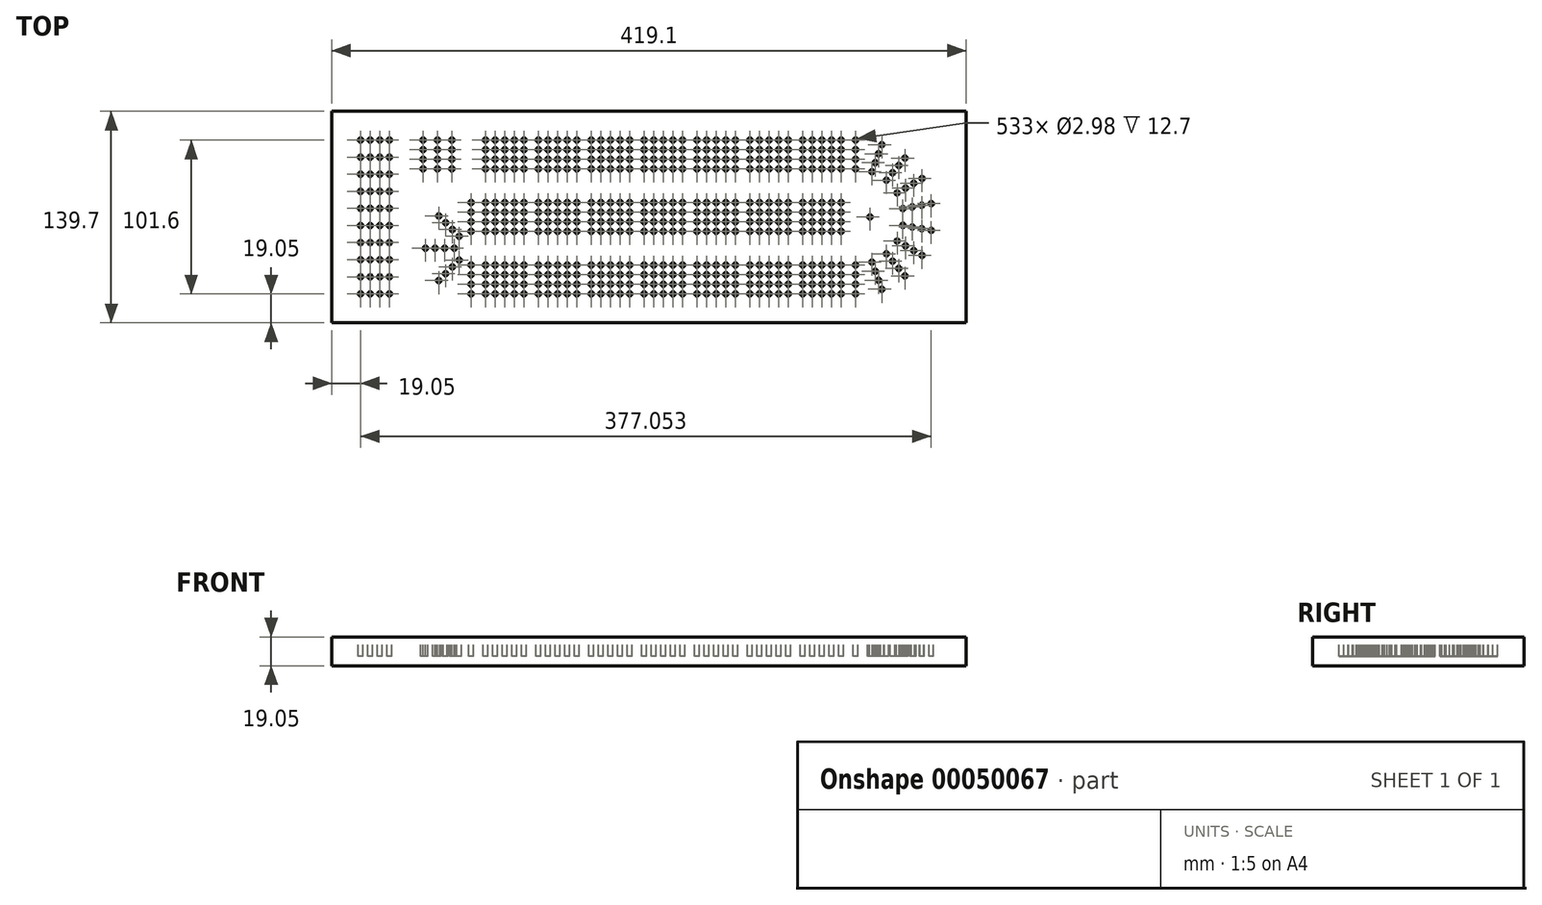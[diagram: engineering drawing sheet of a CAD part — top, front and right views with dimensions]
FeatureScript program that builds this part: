
annotation { "Feature Type Name" : "Feature", "Feature Type Description" : "" }
export const myFeature = defineFeature(function(context is Context, id is Id, definition is map)
    precondition{}
    {
        {
            var Q0;
            Q0=qCreatedBy(makeId("Top.planeOp"),FACE);
            var sketch = newSketch(context, id + "F0", { "sketchPlane" : qUnion([Q0])});
            skLineSegment(sketch, "E0.bottom", {"start": v(0, 0) * mm, "end": v(419.1, 0) * mm});
            skLineSegment(sketch, "E0.top", {"start": v(0, 139.7) * mm, "end": v(419.1, 139.7) * mm});
            skLineSegment(sketch, "E0.left", {"start": v(0, 0) * mm, "end": v(0, 139.7) * mm});
            skLineSegment(sketch, "E0.right", {"start": v(419.1, 0) * mm, "end": v(419.1, 139.7) * mm});
            skSolve(sketch);
        }
        {
            var Q0;
            Q0=qSketchRegion(id+"F0",true);
            extrude(context, id + "F1", {"entities" : qUnion([Q0]), "depth" : 19.05 * mm});
        }
        {
            var Q0;
            Q0=makeQuery(id+"F1.opExtrude","CAP_FACE",FACE,{"disambiguationData":[OSD([sQuery(id+"F0.wireOp",EDGE,"E0.bottom"),sQuery(id+"F0.wireOp",EDGE,"E0.top"),sQuery(id+"F0.wireOp",EDGE,"E0.left"),sQuery(id+"F0.wireOp",EDGE,"E0.right")])],"isStart":false});
            var sketch = newSketch(context, id + "F2", { "sketchPlane" : qUnion([Q0])});
            skLineSegment(sketch, "E1", {"start": v(19.05, 139.7) * mm, "end": v(19.05, 120.65) * mm});
            skLineSegment(sketch, "E2", {"start": v(19.05, 120.65) * mm, "end": v(0, 120.65) * mm});
            skCircle(sketch, "E3", {"center": v(19.05, 120.65) * mm, "radius": 1.49 * mm});
            skCircle(sketch, "E4.0.1.0", {"center": v(19.05, 109.36) * mm, "radius": 1.49 * mm});
            skCircle(sketch, "E4.0.2.0", {"center": v(19.05, 98.07) * mm, "radius": 1.49 * mm});
            skCircle(sketch, "E4.0.3.0", {"center": v(19.05, 86.78) * mm, "radius": 1.49 * mm});
            skCircle(sketch, "E4.0.4.0", {"center": v(19.05, 75.5) * mm, "radius": 1.49 * mm});
            skCircle(sketch, "E4.0.5.0", {"center": v(19.05, 64.2) * mm, "radius": 1.49 * mm});
            skCircle(sketch, "E4.0.6.0", {"center": v(19.05, 52.92) * mm, "radius": 1.49 * mm});
            skCircle(sketch, "E4.0.7.0", {"center": v(19.05, 41.63) * mm, "radius": 1.49 * mm});
            skCircle(sketch, "E4.0.8.0", {"center": v(19.05, 30.34) * mm, "radius": 1.49 * mm});
            skCircle(sketch, "E4.0.9.0", {"center": v(19.05, 19.05) * mm, "radius": 1.49 * mm});
            skCircle(sketch, "E4.1.0.0", {"center": v(25.4, 120.65) * mm, "radius": 1.49 * mm});
            skCircle(sketch, "E4.1.1.0", {"center": v(25.4, 109.36) * mm, "radius": 1.49 * mm});
            skCircle(sketch, "E4.1.2.0", {"center": v(25.4, 98.07) * mm, "radius": 1.49 * mm});
            skCircle(sketch, "E4.1.3.0", {"center": v(25.4, 86.78) * mm, "radius": 1.49 * mm});
            skCircle(sketch, "E4.1.4.0", {"center": v(25.4, 75.5) * mm, "radius": 1.49 * mm});
            skCircle(sketch, "E4.1.5.0", {"center": v(25.4, 64.2) * mm, "radius": 1.49 * mm});
            skCircle(sketch, "E4.1.6.0", {"center": v(25.4, 52.92) * mm, "radius": 1.49 * mm});
            skCircle(sketch, "E4.1.7.0", {"center": v(25.4, 41.63) * mm, "radius": 1.49 * mm});
            skCircle(sketch, "E4.1.8.0", {"center": v(25.4, 30.34) * mm, "radius": 1.49 * mm});
            skCircle(sketch, "E4.1.9.0", {"center": v(25.4, 19.05) * mm, "radius": 1.49 * mm});
            skCircle(sketch, "E4.2.0.0", {"center": v(31.75, 120.65) * mm, "radius": 1.49 * mm});
            skCircle(sketch, "E4.2.1.0", {"center": v(31.75, 109.36) * mm, "radius": 1.49 * mm});
            skCircle(sketch, "E4.2.2.0", {"center": v(31.75, 98.07) * mm, "radius": 1.49 * mm});
            skCircle(sketch, "E4.2.3.0", {"center": v(31.75, 86.78) * mm, "radius": 1.49 * mm});
            skCircle(sketch, "E4.2.4.0", {"center": v(31.75, 75.5) * mm, "radius": 1.49 * mm});
            skCircle(sketch, "E4.2.5.0", {"center": v(31.75, 64.2) * mm, "radius": 1.49 * mm});
            skCircle(sketch, "E4.2.6.0", {"center": v(31.75, 52.92) * mm, "radius": 1.49 * mm});
            skCircle(sketch, "E4.2.7.0", {"center": v(31.75, 41.63) * mm, "radius": 1.49 * mm});
            skCircle(sketch, "E4.2.8.0", {"center": v(31.75, 30.34) * mm, "radius": 1.49 * mm});
            skCircle(sketch, "E4.2.9.0", {"center": v(31.75, 19.05) * mm, "radius": 1.49 * mm});
            skCircle(sketch, "E4.3.0.0", {"center": v(38.1, 120.65) * mm, "radius": 1.49 * mm});
            skCircle(sketch, "E4.3.1.0", {"center": v(38.1, 109.36) * mm, "radius": 1.49 * mm});
            skCircle(sketch, "E4.3.2.0", {"center": v(38.1, 98.07) * mm, "radius": 1.49 * mm});
            skCircle(sketch, "E4.3.3.0", {"center": v(38.1, 86.78) * mm, "radius": 1.49 * mm});
            skCircle(sketch, "E4.3.4.0", {"center": v(38.1, 75.5) * mm, "radius": 1.49 * mm});
            skCircle(sketch, "E4.3.5.0", {"center": v(38.1, 64.2) * mm, "radius": 1.49 * mm});
            skCircle(sketch, "E4.3.6.0", {"center": v(38.1, 52.92) * mm, "radius": 1.49 * mm});
            skCircle(sketch, "E4.3.7.0", {"center": v(38.1, 41.63) * mm, "radius": 1.49 * mm});
            skCircle(sketch, "E4.3.8.0", {"center": v(38.1, 30.34) * mm, "radius": 1.49 * mm});
            skCircle(sketch, "E4.3.9.0", {"center": v(38.1, 19.05) * mm, "radius": 1.49 * mm});
            skLineSegment(sketch, "E4.direction1", {"start": v(19.05, 120.65) * mm, "end": v(25.4, 120.65) * mm, "construction": true});
            skLineSegment(sketch, "E4.direction2", {"start": v(19.05, 120.65) * mm, "end": v(19.05, 109.36) * mm, "construction": true});
            skCircle(sketch, "E5", {"center": v(60.32, 120.65) * mm, "radius": 1.49 * mm});
            skCircle(sketch, "E6.0.1.0", {"center": v(60.32, 114.3) * mm, "radius": 1.49 * mm});
            skCircle(sketch, "E6.0.2.0", {"center": v(60.32, 107.95) * mm, "radius": 1.49 * mm});
            skCircle(sketch, "E6.0.3.0", {"center": v(60.32, 101.6) * mm, "radius": 1.49 * mm});
            skCircle(sketch, "E6.1.0.0", {"center": v(69.85, 120.65) * mm, "radius": 1.49 * mm});
            skCircle(sketch, "E6.1.1.0", {"center": v(69.85, 114.3) * mm, "radius": 1.49 * mm});
            skCircle(sketch, "E6.1.2.0", {"center": v(69.85, 107.95) * mm, "radius": 1.49 * mm});
            skCircle(sketch, "E6.1.3.0", {"center": v(69.85, 101.6) * mm, "radius": 1.49 * mm});
            skCircle(sketch, "E6.2.0.0", {"center": v(79.38, 120.65) * mm, "radius": 1.49 * mm});
            skCircle(sketch, "E6.2.1.0", {"center": v(79.38, 114.3) * mm, "radius": 1.49 * mm});
            skCircle(sketch, "E6.2.2.0", {"center": v(79.38, 107.95) * mm, "radius": 1.49 * mm});
            skCircle(sketch, "E6.2.3.0", {"center": v(79.38, 101.6) * mm, "radius": 1.49 * mm});
            skLineSegment(sketch, "E6.direction1", {"start": v(60.32, 120.65) * mm, "end": v(69.85, 120.65) * mm, "construction": true});
            skLineSegment(sketch, "E6.direction2", {"start": v(60.32, 120.65) * mm, "end": v(60.32, 114.3) * mm, "construction": true});
            skCircle(sketch, "E7", {"center": v(101.6, 120.65) * mm, "radius": 1.49 * mm});
            skCircle(sketch, "E8.0.1.0", {"center": v(101.6, 114.3) * mm, "radius": 1.49 * mm});
            skCircle(sketch, "E8.0.2.0", {"center": v(101.6, 107.95) * mm, "radius": 1.49 * mm});
            skCircle(sketch, "E8.0.3.0", {"center": v(101.6, 101.6) * mm, "radius": 1.49 * mm});
            skCircle(sketch, "E8.1.0.0", {"center": v(107.95, 120.65) * mm, "radius": 1.49 * mm});
            skCircle(sketch, "E8.1.1.0", {"center": v(107.95, 114.3) * mm, "radius": 1.49 * mm});
            skCircle(sketch, "E8.1.2.0", {"center": v(107.95, 107.95) * mm, "radius": 1.49 * mm});
            skCircle(sketch, "E8.1.3.0", {"center": v(107.95, 101.6) * mm, "radius": 1.49 * mm});
            skCircle(sketch, "E8.2.0.0", {"center": v(114.3, 120.65) * mm, "radius": 1.49 * mm});
            skCircle(sketch, "E8.2.1.0", {"center": v(114.3, 114.3) * mm, "radius": 1.49 * mm});
            skCircle(sketch, "E8.2.2.0", {"center": v(114.3, 107.95) * mm, "radius": 1.49 * mm});
            skCircle(sketch, "E8.2.3.0", {"center": v(114.3, 101.6) * mm, "radius": 1.49 * mm});
            skCircle(sketch, "E8.3.0.0", {"center": v(120.65, 120.65) * mm, "radius": 1.49 * mm});
            skCircle(sketch, "E8.3.1.0", {"center": v(120.65, 114.3) * mm, "radius": 1.49 * mm});
            skCircle(sketch, "E8.3.2.0", {"center": v(120.65, 107.95) * mm, "radius": 1.49 * mm});
            skCircle(sketch, "E8.3.3.0", {"center": v(120.65, 101.6) * mm, "radius": 1.49 * mm});
            skCircle(sketch, "E8.4.0.0", {"center": v(127, 120.65) * mm, "radius": 1.49 * mm});
            skCircle(sketch, "E8.4.1.0", {"center": v(127, 114.3) * mm, "radius": 1.49 * mm});
            skCircle(sketch, "E8.4.2.0", {"center": v(127, 107.95) * mm, "radius": 1.49 * mm});
            skCircle(sketch, "E8.4.3.0", {"center": v(127, 101.6) * mm, "radius": 1.49 * mm});
            skLineSegment(sketch, "E8.direction1", {"start": v(101.6, 120.65) * mm, "end": v(107.95, 120.65) * mm, "construction": true});
            skLineSegment(sketch, "E8.direction2", {"start": v(101.6, 120.65) * mm, "end": v(101.6, 114.3) * mm, "construction": true});
            skCircle(sketch, "E9.1.0.0", {"center": v(149.22, 114.3) * mm, "radius": 1.49 * mm});
            skCircle(sketch, "E9.1.0.1", {"center": v(136.53, 107.95) * mm, "radius": 1.49 * mm});
            skCircle(sketch, "E9.1.0.2", {"center": v(161.92, 107.95) * mm, "radius": 1.49 * mm});
            skCircle(sketch, "E9.1.0.3", {"center": v(149.22, 120.65) * mm, "radius": 1.49 * mm});
            skCircle(sketch, "E9.1.0.4", {"center": v(161.92, 114.3) * mm, "radius": 1.49 * mm});
            skCircle(sketch, "E9.1.0.5", {"center": v(161.92, 120.65) * mm, "radius": 1.49 * mm});
            skCircle(sketch, "E9.1.0.6", {"center": v(142.88, 101.6) * mm, "radius": 1.49 * mm});
            skCircle(sketch, "E9.1.0.7", {"center": v(155.57, 107.95) * mm, "radius": 1.49 * mm});
            skCircle(sketch, "E9.1.0.8", {"center": v(142.88, 107.95) * mm, "radius": 1.49 * mm});
            skCircle(sketch, "E9.1.0.9", {"center": v(155.57, 101.6) * mm, "radius": 1.49 * mm});
            skCircle(sketch, "E9.1.0.10", {"center": v(155.57, 114.3) * mm, "radius": 1.49 * mm});
            skCircle(sketch, "E9.1.0.11", {"center": v(149.22, 107.95) * mm, "radius": 1.49 * mm});
            skCircle(sketch, "E9.1.0.12", {"center": v(149.22, 101.6) * mm, "radius": 1.49 * mm});
            skCircle(sketch, "E9.1.0.13", {"center": v(161.92, 101.6) * mm, "radius": 1.49 * mm});
            skCircle(sketch, "E9.1.0.14", {"center": v(136.53, 101.6) * mm, "radius": 1.49 * mm});
            skCircle(sketch, "E9.1.0.15", {"center": v(155.57, 120.65) * mm, "radius": 1.49 * mm});
            skCircle(sketch, "E9.1.0.16", {"center": v(142.88, 114.3) * mm, "radius": 1.49 * mm});
            skCircle(sketch, "E9.1.0.17", {"center": v(136.53, 114.3) * mm, "radius": 1.49 * mm});
            skCircle(sketch, "E9.1.0.18", {"center": v(142.88, 120.65) * mm, "radius": 1.49 * mm});
            skLineSegment(sketch, "E9.1.0.19", {"start": v(136.53, 120.65) * mm, "end": v(136.53, 114.3) * mm, "construction": true});
            skCircle(sketch, "E9.1.0.20", {"center": v(136.53, 120.65) * mm, "radius": 1.49 * mm});
            skLineSegment(sketch, "E9.1.0.21", {"start": v(136.53, 120.65) * mm, "end": v(142.87, 120.65) * mm, "construction": true});
            skCircle(sketch, "E9.2.0.0", {"center": v(184.15, 114.3) * mm, "radius": 1.49 * mm});
            skCircle(sketch, "E9.2.0.1", {"center": v(171.45, 107.95) * mm, "radius": 1.49 * mm});
            skCircle(sketch, "E9.2.0.2", {"center": v(196.85, 107.95) * mm, "radius": 1.49 * mm});
            skCircle(sketch, "E9.2.0.3", {"center": v(184.15, 120.65) * mm, "radius": 1.49 * mm});
            skCircle(sketch, "E9.2.0.4", {"center": v(196.85, 114.3) * mm, "radius": 1.49 * mm});
            skCircle(sketch, "E9.2.0.5", {"center": v(196.85, 120.65) * mm, "radius": 1.49 * mm});
            skCircle(sketch, "E9.2.0.6", {"center": v(177.8, 101.6) * mm, "radius": 1.49 * mm});
            skCircle(sketch, "E9.2.0.7", {"center": v(190.5, 107.95) * mm, "radius": 1.49 * mm});
            skCircle(sketch, "E9.2.0.8", {"center": v(177.8, 107.95) * mm, "radius": 1.49 * mm});
            skCircle(sketch, "E9.2.0.9", {"center": v(190.5, 101.6) * mm, "radius": 1.49 * mm});
            skCircle(sketch, "E9.2.0.10", {"center": v(190.5, 114.3) * mm, "radius": 1.49 * mm});
            skCircle(sketch, "E9.2.0.11", {"center": v(184.15, 107.95) * mm, "radius": 1.49 * mm});
            skCircle(sketch, "E9.2.0.12", {"center": v(184.15, 101.6) * mm, "radius": 1.49 * mm});
            skCircle(sketch, "E9.2.0.13", {"center": v(196.85, 101.6) * mm, "radius": 1.49 * mm});
            skCircle(sketch, "E9.2.0.14", {"center": v(171.45, 101.6) * mm, "radius": 1.49 * mm});
            skCircle(sketch, "E9.2.0.15", {"center": v(190.5, 120.65) * mm, "radius": 1.49 * mm});
            skCircle(sketch, "E9.2.0.16", {"center": v(177.8, 114.3) * mm, "radius": 1.49 * mm});
            skCircle(sketch, "E9.2.0.17", {"center": v(171.45, 114.3) * mm, "radius": 1.49 * mm});
            skCircle(sketch, "E9.2.0.18", {"center": v(177.8, 120.65) * mm, "radius": 1.49 * mm});
            skLineSegment(sketch, "E9.2.0.19", {"start": v(171.45, 120.65) * mm, "end": v(171.45, 114.3) * mm, "construction": true});
            skCircle(sketch, "E9.2.0.20", {"center": v(171.45, 120.65) * mm, "radius": 1.49 * mm});
            skLineSegment(sketch, "E9.2.0.21", {"start": v(171.45, 120.65) * mm, "end": v(177.8, 120.65) * mm, "construction": true});
            skCircle(sketch, "E9.3.0.0", {"center": v(219.08, 114.3) * mm, "radius": 1.49 * mm});
            skCircle(sketch, "E9.3.0.1", {"center": v(206.38, 107.95) * mm, "radius": 1.49 * mm});
            skCircle(sketch, "E9.3.0.2", {"center": v(231.78, 107.95) * mm, "radius": 1.49 * mm});
            skCircle(sketch, "E9.3.0.3", {"center": v(219.08, 120.65) * mm, "radius": 1.49 * mm});
            skCircle(sketch, "E9.3.0.4", {"center": v(231.78, 114.3) * mm, "radius": 1.49 * mm});
            skCircle(sketch, "E9.3.0.5", {"center": v(231.78, 120.65) * mm, "radius": 1.49 * mm});
            skCircle(sketch, "E9.3.0.6", {"center": v(212.73, 101.6) * mm, "radius": 1.49 * mm});
            skCircle(sketch, "E9.3.0.7", {"center": v(225.43, 107.95) * mm, "radius": 1.49 * mm});
            skCircle(sketch, "E9.3.0.8", {"center": v(212.73, 107.95) * mm, "radius": 1.49 * mm});
            skCircle(sketch, "E9.3.0.9", {"center": v(225.43, 101.6) * mm, "radius": 1.49 * mm});
            skCircle(sketch, "E9.3.0.10", {"center": v(225.43, 114.3) * mm, "radius": 1.49 * mm});
            skCircle(sketch, "E9.3.0.11", {"center": v(219.08, 107.95) * mm, "radius": 1.49 * mm});
            skCircle(sketch, "E9.3.0.12", {"center": v(219.08, 101.6) * mm, "radius": 1.49 * mm});
            skCircle(sketch, "E9.3.0.13", {"center": v(231.78, 101.6) * mm, "radius": 1.49 * mm});
            skCircle(sketch, "E9.3.0.14", {"center": v(206.38, 101.6) * mm, "radius": 1.49 * mm});
            skCircle(sketch, "E9.3.0.15", {"center": v(225.43, 120.65) * mm, "radius": 1.49 * mm});
            skCircle(sketch, "E9.3.0.16", {"center": v(212.73, 114.3) * mm, "radius": 1.49 * mm});
            skCircle(sketch, "E9.3.0.17", {"center": v(206.38, 114.3) * mm, "radius": 1.49 * mm});
            skCircle(sketch, "E9.3.0.18", {"center": v(212.73, 120.65) * mm, "radius": 1.49 * mm});
            skLineSegment(sketch, "E9.3.0.19", {"start": v(206.38, 120.65) * mm, "end": v(206.38, 114.3) * mm, "construction": true});
            skCircle(sketch, "E9.3.0.20", {"center": v(206.38, 120.65) * mm, "radius": 1.49 * mm});
            skLineSegment(sketch, "E9.3.0.21", {"start": v(206.38, 120.65) * mm, "end": v(212.72, 120.65) * mm, "construction": true});
            skCircle(sketch, "E9.4.0.0", {"center": v(254, 114.3) * mm, "radius": 1.49 * mm});
            skCircle(sketch, "E9.4.0.1", {"center": v(241.3, 107.95) * mm, "radius": 1.49 * mm});
            skCircle(sketch, "E9.4.0.2", {"center": v(266.7, 107.95) * mm, "radius": 1.49 * mm});
            skCircle(sketch, "E9.4.0.3", {"center": v(254, 120.65) * mm, "radius": 1.49 * mm});
            skCircle(sketch, "E9.4.0.4", {"center": v(266.7, 114.3) * mm, "radius": 1.49 * mm});
            skCircle(sketch, "E9.4.0.5", {"center": v(266.7, 120.65) * mm, "radius": 1.49 * mm});
            skCircle(sketch, "E9.4.0.6", {"center": v(247.65, 101.6) * mm, "radius": 1.49 * mm});
            skCircle(sketch, "E9.4.0.7", {"center": v(260.35, 107.95) * mm, "radius": 1.49 * mm});
            skCircle(sketch, "E9.4.0.8", {"center": v(247.65, 107.95) * mm, "radius": 1.49 * mm});
            skCircle(sketch, "E9.4.0.9", {"center": v(260.35, 101.6) * mm, "radius": 1.49 * mm});
            skCircle(sketch, "E9.4.0.10", {"center": v(260.35, 114.3) * mm, "radius": 1.49 * mm});
            skCircle(sketch, "E9.4.0.11", {"center": v(254, 107.95) * mm, "radius": 1.49 * mm});
            skCircle(sketch, "E9.4.0.12", {"center": v(254, 101.6) * mm, "radius": 1.49 * mm});
            skCircle(sketch, "E9.4.0.13", {"center": v(266.7, 101.6) * mm, "radius": 1.49 * mm});
            skCircle(sketch, "E9.4.0.14", {"center": v(241.3, 101.6) * mm, "radius": 1.49 * mm});
            skCircle(sketch, "E9.4.0.15", {"center": v(260.35, 120.65) * mm, "radius": 1.49 * mm});
            skCircle(sketch, "E9.4.0.16", {"center": v(247.65, 114.3) * mm, "radius": 1.49 * mm});
            skCircle(sketch, "E9.4.0.17", {"center": v(241.3, 114.3) * mm, "radius": 1.49 * mm});
            skCircle(sketch, "E9.4.0.18", {"center": v(247.65, 120.65) * mm, "radius": 1.49 * mm});
            skLineSegment(sketch, "E9.4.0.19", {"start": v(241.3, 120.65) * mm, "end": v(241.3, 114.3) * mm, "construction": true});
            skCircle(sketch, "E9.4.0.20", {"center": v(241.3, 120.65) * mm, "radius": 1.49 * mm});
            skLineSegment(sketch, "E9.4.0.21", {"start": v(241.3, 120.65) * mm, "end": v(247.65, 120.65) * mm, "construction": true});
            skLineSegment(sketch, "E9.direction1", {"start": v(114.3, 114.3) * mm, "end": v(149.22, 114.3) * mm, "construction": true});
            skCircle(sketch, "E10.0.5.0", {"center": v(288.93, 114.3) * mm, "radius": 1.49 * mm});
            skCircle(sketch, "E10.2.5.0", {"center": v(276.23, 107.95) * mm, "radius": 1.49 * mm});
            skCircle(sketch, "E10.4.5.0", {"center": v(301.63, 107.95) * mm, "radius": 1.49 * mm});
            skCircle(sketch, "E10.6.5.0", {"center": v(288.93, 120.65) * mm, "radius": 1.49 * mm});
            skCircle(sketch, "E10.8.5.0", {"center": v(301.63, 114.3) * mm, "radius": 1.49 * mm});
            skCircle(sketch, "E10.10.5.0", {"center": v(301.63, 120.65) * mm, "radius": 1.49 * mm});
            skCircle(sketch, "E10.12.5.0", {"center": v(282.58, 101.6) * mm, "radius": 1.49 * mm});
            skCircle(sketch, "E10.14.5.0", {"center": v(295.28, 107.95) * mm, "radius": 1.49 * mm});
            skCircle(sketch, "E10.16.5.0", {"center": v(282.58, 107.95) * mm, "radius": 1.49 * mm});
            skCircle(sketch, "E10.18.5.0", {"center": v(295.28, 101.6) * mm, "radius": 1.49 * mm});
            skCircle(sketch, "E10.20.5.0", {"center": v(295.28, 114.3) * mm, "radius": 1.49 * mm});
            skCircle(sketch, "E10.22.5.0", {"center": v(288.93, 107.95) * mm, "radius": 1.49 * mm});
            skCircle(sketch, "E10.24.5.0", {"center": v(288.93, 101.6) * mm, "radius": 1.49 * mm});
            skCircle(sketch, "E10.26.5.0", {"center": v(301.63, 101.6) * mm, "radius": 1.49 * mm});
            skCircle(sketch, "E10.28.5.0", {"center": v(276.23, 101.6) * mm, "radius": 1.49 * mm});
            skCircle(sketch, "E10.30.5.0", {"center": v(295.28, 120.65) * mm, "radius": 1.49 * mm});
            skCircle(sketch, "E10.32.5.0", {"center": v(282.58, 114.3) * mm, "radius": 1.49 * mm});
            skCircle(sketch, "E10.34.5.0", {"center": v(276.23, 114.3) * mm, "radius": 1.49 * mm});
            skCircle(sketch, "E10.36.5.0", {"center": v(282.58, 120.65) * mm, "radius": 1.49 * mm});
            skLineSegment(sketch, "E10.38.5.0", {"start": v(276.23, 120.65) * mm, "end": v(276.23, 114.3) * mm, "construction": true});
            skCircle(sketch, "E10.41.5.0", {"center": v(276.23, 120.65) * mm, "radius": 1.49 * mm});
            skLineSegment(sketch, "E10.43.5.0", {"start": v(276.23, 120.65) * mm, "end": v(282.58, 120.65) * mm, "construction": true});
            skCircle(sketch, "E10.0.6.0", {"center": v(323.85, 114.3) * mm, "radius": 1.49 * mm});
            skCircle(sketch, "E10.2.6.0", {"center": v(311.15, 107.95) * mm, "radius": 1.49 * mm});
            skCircle(sketch, "E10.4.6.0", {"center": v(336.55, 107.95) * mm, "radius": 1.49 * mm});
            skCircle(sketch, "E10.6.6.0", {"center": v(323.85, 120.65) * mm, "radius": 1.49 * mm});
            skCircle(sketch, "E10.8.6.0", {"center": v(336.55, 114.3) * mm, "radius": 1.49 * mm});
            skCircle(sketch, "E10.10.6.0", {"center": v(336.55, 120.65) * mm, "radius": 1.49 * mm});
            skCircle(sketch, "E10.12.6.0", {"center": v(317.5, 101.6) * mm, "radius": 1.49 * mm});
            skCircle(sketch, "E10.14.6.0", {"center": v(330.2, 107.95) * mm, "radius": 1.49 * mm});
            skCircle(sketch, "E10.16.6.0", {"center": v(317.5, 107.95) * mm, "radius": 1.49 * mm});
            skCircle(sketch, "E10.18.6.0", {"center": v(330.2, 101.6) * mm, "radius": 1.49 * mm});
            skCircle(sketch, "E10.20.6.0", {"center": v(330.2, 114.3) * mm, "radius": 1.49 * mm});
            skCircle(sketch, "E10.22.6.0", {"center": v(323.85, 107.95) * mm, "radius": 1.49 * mm});
            skCircle(sketch, "E10.24.6.0", {"center": v(323.85, 101.6) * mm, "radius": 1.49 * mm});
            skCircle(sketch, "E10.26.6.0", {"center": v(336.55, 101.6) * mm, "radius": 1.49 * mm});
            skCircle(sketch, "E10.28.6.0", {"center": v(311.15, 101.6) * mm, "radius": 1.49 * mm});
            skCircle(sketch, "E10.30.6.0", {"center": v(330.2, 120.65) * mm, "radius": 1.49 * mm});
            skCircle(sketch, "E10.32.6.0", {"center": v(317.5, 114.3) * mm, "radius": 1.49 * mm});
            skCircle(sketch, "E10.34.6.0", {"center": v(311.15, 114.3) * mm, "radius": 1.49 * mm});
            skCircle(sketch, "E10.36.6.0", {"center": v(317.5, 120.65) * mm, "radius": 1.49 * mm});
            skLineSegment(sketch, "E10.38.6.0", {"start": v(311.15, 120.65) * mm, "end": v(311.15, 114.3) * mm, "construction": true});
            skCircle(sketch, "E10.41.6.0", {"center": v(311.15, 120.65) * mm, "radius": 1.49 * mm});
            skLineSegment(sketch, "E10.43.6.0", {"start": v(311.15, 120.65) * mm, "end": v(317.5, 120.65) * mm, "construction": true});
            skCircle(sketch, "E11.0.1.0", {"center": v(219.08, 66.68) * mm, "radius": 1.49 * mm});
            skCircle(sketch, "E11.0.1.1", {"center": v(171.45, 66.68) * mm, "radius": 1.49 * mm});
            skCircle(sketch, "E11.0.1.2", {"center": v(155.57, 66.68) * mm, "radius": 1.49 * mm});
            skCircle(sketch, "E11.0.1.3", {"center": v(317.5, 66.68) * mm, "radius": 1.49 * mm});
            skCircle(sketch, "E11.0.1.4", {"center": v(276.23, 60.33) * mm, "radius": 1.49 * mm});
            skCircle(sketch, "E11.0.1.5", {"center": v(266.7, 79.38) * mm, "radius": 1.49 * mm});
            skCircle(sketch, "E11.0.1.6", {"center": v(155.57, 60.33) * mm, "radius": 1.49 * mm});
            skCircle(sketch, "E11.0.1.7", {"center": v(120.65, 60.33) * mm, "radius": 1.49 * mm});
            skCircle(sketch, "E11.0.1.8", {"center": v(260.35, 66.68) * mm, "radius": 1.49 * mm});
            skCircle(sketch, "E11.0.1.9", {"center": v(231.78, 60.33) * mm, "radius": 1.49 * mm});
            skCircle(sketch, "E11.0.1.10", {"center": v(184.15, 79.38) * mm, "radius": 1.49 * mm});
            skCircle(sketch, "E11.0.1.11", {"center": v(330.2, 73.03) * mm, "radius": 1.49 * mm});
            skCircle(sketch, "E11.0.1.12", {"center": v(282.58, 73.03) * mm, "radius": 1.49 * mm});
            skCircle(sketch, "E11.0.1.13", {"center": v(288.93, 73.03) * mm, "radius": 1.49 * mm});
            skCircle(sketch, "E11.0.1.14", {"center": v(120.65, 66.68) * mm, "radius": 1.49 * mm});
            skCircle(sketch, "E11.0.1.15", {"center": v(219.08, 60.33) * mm, "radius": 1.49 * mm});
            skCircle(sketch, "E11.0.1.16", {"center": v(196.85, 66.68) * mm, "radius": 1.49 * mm});
            skCircle(sketch, "E11.0.1.17", {"center": v(142.88, 66.68) * mm, "radius": 1.49 * mm});
            skCircle(sketch, "E11.0.1.18", {"center": v(330.2, 60.33) * mm, "radius": 1.49 * mm});
            skCircle(sketch, "E11.0.1.19", {"center": v(295.28, 79.38) * mm, "radius": 1.49 * mm});
            skCircle(sketch, "E11.0.1.20", {"center": v(155.57, 73.03) * mm, "radius": 1.49 * mm});
            skCircle(sketch, "E11.0.1.21", {"center": v(206.38, 60.33) * mm, "radius": 1.49 * mm});
            skCircle(sketch, "E11.0.1.22", {"center": v(196.85, 73.03) * mm, "radius": 1.49 * mm});
            skCircle(sketch, "E11.0.1.23", {"center": v(323.85, 66.68) * mm, "radius": 1.49 * mm});
            skCircle(sketch, "E11.0.1.24", {"center": v(276.23, 66.68) * mm, "radius": 1.49 * mm});
            skCircle(sketch, "E11.0.1.25", {"center": v(149.22, 66.68) * mm, "radius": 1.49 * mm});
            skCircle(sketch, "E11.0.1.26", {"center": v(260.35, 60.33) * mm, "radius": 1.49 * mm});
            skCircle(sketch, "E11.0.1.27", {"center": v(196.85, 79.38) * mm, "radius": 1.49 * mm});
            skCircle(sketch, "E11.0.1.28", {"center": v(323.85, 60.33) * mm, "radius": 1.49 * mm});
            skCircle(sketch, "E11.0.1.29", {"center": v(301.63, 66.68) * mm, "radius": 1.49 * mm});
            skCircle(sketch, "E11.0.1.30", {"center": v(149.22, 60.33) * mm, "radius": 1.49 * mm});
            skCircle(sketch, "E11.0.1.31", {"center": v(127, 66.68) * mm, "radius": 1.49 * mm});
            skCircle(sketch, "E11.0.1.32", {"center": v(101.6, 66.68) * mm, "radius": 1.49 * mm});
            skCircle(sketch, "E11.0.1.33", {"center": v(177.8, 60.33) * mm, "radius": 1.49 * mm});
            skCircle(sketch, "E11.0.1.34", {"center": v(336.55, 60.33) * mm, "radius": 1.49 * mm});
            skCircle(sketch, "E11.0.1.35", {"center": v(288.93, 79.38) * mm, "radius": 1.49 * mm});
            skCircle(sketch, "E11.0.1.36", {"center": v(254, 66.68) * mm, "radius": 1.49 * mm});
            skCircle(sketch, "E11.0.1.37", {"center": v(206.38, 66.68) * mm, "radius": 1.49 * mm});
            skCircle(sketch, "E11.0.1.38", {"center": v(190.5, 66.68) * mm, "radius": 1.49 * mm});
            skCircle(sketch, "E11.0.1.39", {"center": v(311.15, 60.33) * mm, "radius": 1.49 * mm});
            skCircle(sketch, "E11.0.1.40", {"center": v(161.92, 60.33) * mm, "radius": 1.49 * mm});
            skCircle(sketch, "E11.0.1.41", {"center": v(127, 60.33) * mm, "radius": 1.49 * mm});
            skCircle(sketch, "E11.0.1.42", {"center": v(101.6, 60.33) * mm, "radius": 1.49 * mm});
            skCircle(sketch, "E11.0.1.43", {"center": v(330.2, 79.38) * mm, "radius": 1.49 * mm});
            skCircle(sketch, "E11.0.1.44", {"center": v(301.63, 79.38) * mm, "radius": 1.49 * mm});
            skCircle(sketch, "E11.0.1.45", {"center": v(136.53, 60.33) * mm, "radius": 1.49 * mm});
            skCircle(sketch, "E11.0.1.46", {"center": v(254, 60.33) * mm, "radius": 1.49 * mm});
            skCircle(sketch, "E11.0.1.47", {"center": v(231.78, 66.68) * mm, "radius": 1.49 * mm});
            skCircle(sketch, "E11.0.1.48", {"center": v(177.8, 66.68) * mm, "radius": 1.49 * mm});
            skCircle(sketch, "E11.0.1.49", {"center": v(155.57, 79.38) * mm, "radius": 1.49 * mm});
            skCircle(sketch, "E11.0.1.50", {"center": v(266.7, 60.33) * mm, "radius": 1.49 * mm});
            skCircle(sketch, "E11.0.1.51", {"center": v(219.08, 79.38) * mm, "radius": 1.49 * mm});
            skCircle(sketch, "E11.0.1.52", {"center": v(190.5, 60.33) * mm, "radius": 1.49 * mm});
            skCircle(sketch, "E11.0.1.53", {"center": v(282.58, 60.33) * mm, "radius": 1.49 * mm});
            skCircle(sketch, "E11.0.1.54", {"center": v(241.3, 60.33) * mm, "radius": 1.49 * mm});
            skCircle(sketch, "E11.0.1.55", {"center": v(231.78, 73.03) * mm, "radius": 1.49 * mm});
            skCircle(sketch, "E11.0.1.56", {"center": v(190.5, 73.03) * mm, "radius": 1.49 * mm});
            skCircle(sketch, "E11.0.1.57", {"center": v(311.15, 66.68) * mm, "radius": 1.49 * mm});
            skCircle(sketch, "E11.0.1.58", {"center": v(295.28, 66.68) * mm, "radius": 1.49 * mm});
            skCircle(sketch, "E11.0.1.59", {"center": v(136.53, 66.68) * mm, "radius": 1.49 * mm});
            skCircle(sketch, "E11.0.1.60", {"center": v(107.95, 60.33) * mm, "radius": 1.49 * mm});
            skCircle(sketch, "E11.0.1.61", {"center": v(260.35, 79.38) * mm, "radius": 1.49 * mm});
            skCircle(sketch, "E11.0.1.62", {"center": v(231.78, 79.38) * mm, "radius": 1.49 * mm});
            skCircle(sketch, "E11.0.1.63", {"center": v(184.15, 66.68) * mm, "radius": 1.49 * mm});
            skCircle(sketch, "E11.0.1.64", {"center": v(336.55, 66.68) * mm, "radius": 1.49 * mm});
            skCircle(sketch, "E11.0.1.65", {"center": v(282.58, 66.68) * mm, "radius": 1.49 * mm});
            skCircle(sketch, "E11.0.1.66", {"center": v(161.92, 66.68) * mm, "radius": 1.49 * mm});
            skCircle(sketch, "E11.0.1.67", {"center": v(212.73, 60.33) * mm, "radius": 1.49 * mm});
            skCircle(sketch, "E11.0.1.68", {"center": v(184.15, 60.33) * mm, "radius": 1.49 * mm});
            skCircle(sketch, "E11.0.1.69", {"center": v(323.85, 79.38) * mm, "radius": 1.49 * mm});
            skCircle(sketch, "E11.0.1.70", {"center": v(225.43, 66.68) * mm, "radius": 1.49 * mm});
            skCircle(sketch, "E11.0.1.71", {"center": v(196.85, 60.33) * mm, "radius": 1.49 * mm});
            skCircle(sketch, "E11.0.1.72", {"center": v(149.22, 79.38) * mm, "radius": 1.49 * mm});
            skCircle(sketch, "E11.0.1.73", {"center": v(336.55, 73.03) * mm, "radius": 1.49 * mm});
            skCircle(sketch, "E11.0.1.74", {"center": v(295.28, 73.03) * mm, "radius": 1.49 * mm});
            skCircle(sketch, "E11.0.1.75", {"center": v(241.3, 66.68) * mm, "radius": 1.49 * mm});
            skCircle(sketch, "E11.0.1.76", {"center": v(114.3, 66.68) * mm, "radius": 1.49 * mm});
            skCircle(sketch, "E11.0.1.77", {"center": v(212.73, 66.68) * mm, "radius": 1.49 * mm});
            skCircle(sketch, "E11.0.1.78", {"center": v(171.45, 60.33) * mm, "radius": 1.49 * mm});
            skCircle(sketch, "E11.0.1.79", {"center": v(336.55, 79.38) * mm, "radius": 1.49 * mm});
            skCircle(sketch, "E11.0.1.80", {"center": v(288.93, 66.68) * mm, "radius": 1.49 * mm});
            skCircle(sketch, "E11.0.1.81", {"center": v(266.7, 66.68) * mm, "radius": 1.49 * mm});
            skCircle(sketch, "E11.0.1.82", {"center": v(190.5, 79.38) * mm, "radius": 1.49 * mm});
            skCircle(sketch, "E11.0.1.83", {"center": v(161.92, 79.38) * mm, "radius": 1.49 * mm});
            skCircle(sketch, "E11.0.1.84", {"center": v(317.5, 60.33) * mm, "radius": 1.49 * mm});
            skCircle(sketch, "E11.0.1.85", {"center": v(288.93, 60.33) * mm, "radius": 1.49 * mm});
            skCircle(sketch, "E11.0.1.86", {"center": v(254, 79.38) * mm, "radius": 1.49 * mm});
            skCircle(sketch, "E11.0.1.87", {"center": v(330.2, 66.68) * mm, "radius": 1.49 * mm});
            skCircle(sketch, "E11.0.1.88", {"center": v(301.63, 60.33) * mm, "radius": 1.49 * mm});
            skCircle(sketch, "E11.0.1.89", {"center": v(266.7, 73.03) * mm, "radius": 1.49 * mm});
            skCircle(sketch, "E11.0.1.90", {"center": v(120.65, 73.03) * mm, "radius": 1.49 * mm});
            skCircle(sketch, "E11.0.1.91", {"center": v(171.45, 73.03) * mm, "radius": 1.49 * mm});
            skLineSegment(sketch, "E11.0.1.92", {"start": v(114.3, 73.03) * mm, "end": v(149.22, 73.03) * mm, "construction": true});
            skCircle(sketch, "E11.0.1.93", {"center": v(247.65, 60.33) * mm, "radius": 1.49 * mm});
            skCircle(sketch, "E11.0.1.94", {"center": v(127, 79.38) * mm, "radius": 1.49 * mm});
            skCircle(sketch, "E11.0.1.95", {"center": v(247.65, 66.68) * mm, "radius": 1.49 * mm});
            skCircle(sketch, "E11.0.1.96", {"center": v(127, 73.03) * mm, "radius": 1.49 * mm});
            skCircle(sketch, "E11.0.1.97", {"center": v(225.43, 79.38) * mm, "radius": 1.49 * mm});
            skCircle(sketch, "E11.0.1.98", {"center": v(282.58, 79.38) * mm, "radius": 1.49 * mm});
            skCircle(sketch, "E11.0.1.99", {"center": v(260.35, 73.03) * mm, "radius": 1.49 * mm});
            skCircle(sketch, "E11.0.1.100", {"center": v(212.73, 73.03) * mm, "radius": 1.49 * mm});
            skCircle(sketch, "E11.0.1.101", {"center": v(219.08, 73.03) * mm, "radius": 1.49 * mm});
            skCircle(sketch, "E11.0.1.102", {"center": v(301.63, 73.03) * mm, "radius": 1.49 * mm});
            skCircle(sketch, "E11.0.1.103", {"center": v(212.73, 79.38) * mm, "radius": 1.49 * mm});
            skCircle(sketch, "E11.0.1.104", {"center": v(323.85, 73.03) * mm, "radius": 1.49 * mm});
            skCircle(sketch, "E11.0.1.105", {"center": v(142.88, 73.03) * mm, "radius": 1.49 * mm});
            skCircle(sketch, "E11.0.1.106", {"center": v(149.22, 73.03) * mm, "radius": 1.49 * mm});
            skCircle(sketch, "E11.0.1.107", {"center": v(107.95, 66.68) * mm, "radius": 1.49 * mm});
            skCircle(sketch, "E11.0.1.108", {"center": v(247.65, 73.03) * mm, "radius": 1.49 * mm});
            skCircle(sketch, "E11.0.1.109", {"center": v(254, 73.03) * mm, "radius": 1.49 * mm});
            skCircle(sketch, "E11.0.1.110", {"center": v(295.28, 60.33) * mm, "radius": 1.49 * mm});
            skCircle(sketch, "E11.0.1.111", {"center": v(114.3, 73.03) * mm, "radius": 1.49 * mm});
            skCircle(sketch, "E11.0.1.112", {"center": v(241.3, 73.03) * mm, "radius": 1.49 * mm});
            skCircle(sketch, "E11.0.1.113", {"center": v(161.92, 73.03) * mm, "radius": 1.49 * mm});
            skCircle(sketch, "E11.0.1.114", {"center": v(114.3, 60.33) * mm, "radius": 1.49 * mm});
            skCircle(sketch, "E11.0.1.115", {"center": v(225.43, 60.33) * mm, "radius": 1.49 * mm});
            skCircle(sketch, "E11.0.1.116", {"center": v(120.65, 79.38) * mm, "radius": 1.49 * mm});
            skCircle(sketch, "E11.0.1.117", {"center": v(225.43, 73.03) * mm, "radius": 1.49 * mm});
            skCircle(sketch, "E11.0.1.118", {"center": v(177.8, 73.03) * mm, "radius": 1.49 * mm});
            skCircle(sketch, "E11.0.1.119", {"center": v(184.15, 73.03) * mm, "radius": 1.49 * mm});
            skCircle(sketch, "E11.0.1.120", {"center": v(142.88, 60.33) * mm, "radius": 1.49 * mm});
            skLineSegment(sketch, "E11.0.1.121", {"start": v(171.45, 79.38) * mm, "end": v(171.45, 73.03) * mm, "construction": true});
            skCircle(sketch, "E11.0.1.122", {"center": v(177.8, 79.38) * mm, "radius": 1.49 * mm});
            skCircle(sketch, "E11.0.1.123", {"center": v(171.45, 79.38) * mm, "radius": 1.49 * mm});
            skCircle(sketch, "E11.0.1.124", {"center": v(276.23, 73.03) * mm, "radius": 1.49 * mm});
            skCircle(sketch, "E11.0.1.125", {"center": v(101.6, 73.03) * mm, "radius": 1.49 * mm});
            skLineSegment(sketch, "E11.0.1.126", {"start": v(171.45, 79.38) * mm, "end": v(177.8, 79.38) * mm, "construction": true});
            skLineSegment(sketch, "E11.0.1.127", {"start": v(276.23, 79.38) * mm, "end": v(276.23, 73.03) * mm, "construction": true});
            skCircle(sketch, "E11.0.1.128", {"center": v(206.38, 73.03) * mm, "radius": 1.49 * mm});
            skCircle(sketch, "E11.0.1.129", {"center": v(276.23, 79.38) * mm, "radius": 1.49 * mm});
            skLineSegment(sketch, "E11.0.1.130", {"start": v(276.23, 79.38) * mm, "end": v(282.58, 79.38) * mm, "construction": true});
            skCircle(sketch, "E11.0.1.131", {"center": v(107.95, 79.38) * mm, "radius": 1.49 * mm});
            skCircle(sketch, "E11.0.1.132", {"center": v(107.95, 73.03) * mm, "radius": 1.49 * mm});
            skCircle(sketch, "E11.0.1.133", {"center": v(317.5, 73.03) * mm, "radius": 1.49 * mm});
            skCircle(sketch, "E11.0.1.134", {"center": v(206.38, 79.38) * mm, "radius": 1.49 * mm});
            skCircle(sketch, "E11.0.1.135", {"center": v(311.15, 73.03) * mm, "radius": 1.49 * mm});
            skCircle(sketch, "E11.0.1.136", {"center": v(136.53, 73.03) * mm, "radius": 1.49 * mm});
            skLineSegment(sketch, "E11.0.1.137", {"start": v(206.38, 79.38) * mm, "end": v(212.72, 79.38) * mm, "construction": true});
            skCircle(sketch, "E11.0.1.138", {"center": v(317.5, 79.38) * mm, "radius": 1.49 * mm});
            skCircle(sketch, "E11.0.1.139", {"center": v(142.88, 79.38) * mm, "radius": 1.49 * mm});
            skCircle(sketch, "E11.0.1.140", {"center": v(114.3, 79.38) * mm, "radius": 1.49 * mm});
            skLineSegment(sketch, "E11.0.1.141", {"start": v(311.15, 79.38) * mm, "end": v(311.15, 73.03) * mm, "construction": true});
            skCircle(sketch, "E11.0.1.142", {"center": v(311.15, 79.38) * mm, "radius": 1.49 * mm});
            skCircle(sketch, "E11.0.1.143", {"center": v(247.65, 79.38) * mm, "radius": 1.49 * mm});
            skLineSegment(sketch, "E11.0.1.144", {"start": v(311.15, 79.38) * mm, "end": v(317.5, 79.38) * mm, "construction": true});
            skLineSegment(sketch, "E11.0.1.145", {"start": v(241.3, 79.38) * mm, "end": v(241.3, 73.03) * mm, "construction": true});
            skCircle(sketch, "E11.0.1.146", {"center": v(241.3, 79.38) * mm, "radius": 1.49 * mm});
            skLineSegment(sketch, "E11.0.1.147", {"start": v(241.3, 79.38) * mm, "end": v(247.65, 79.38) * mm, "construction": true});
            skCircle(sketch, "E11.0.1.148", {"center": v(101.6, 79.38) * mm, "radius": 1.49 * mm});
            skLineSegment(sketch, "E11.0.1.149", {"start": v(101.6, 79.38) * mm, "end": v(107.95, 79.38) * mm, "construction": true});
            skLineSegment(sketch, "E11.0.1.150", {"start": v(101.6, 79.38) * mm, "end": v(101.6, 73.03) * mm, "construction": true});
            skLineSegment(sketch, "E11.0.1.151", {"start": v(206.38, 79.38) * mm, "end": v(206.38, 73.03) * mm, "construction": true});
            skLineSegment(sketch, "E11.0.1.152", {"start": v(136.53, 79.38) * mm, "end": v(136.53, 73.03) * mm, "construction": true});
            skCircle(sketch, "E11.0.1.153", {"center": v(136.53, 79.38) * mm, "radius": 1.49 * mm});
            skLineSegment(sketch, "E11.0.1.154", {"start": v(136.53, 79.38) * mm, "end": v(142.87, 79.38) * mm, "construction": true});
            skCircle(sketch, "E11.0.2.0", {"center": v(219.08, 25.4) * mm, "radius": 1.49 * mm});
            skCircle(sketch, "E11.0.2.1", {"center": v(171.45, 25.4) * mm, "radius": 1.49 * mm});
            skCircle(sketch, "E11.0.2.2", {"center": v(155.57, 25.4) * mm, "radius": 1.49 * mm});
            skCircle(sketch, "E11.0.2.3", {"center": v(317.5, 25.4) * mm, "radius": 1.49 * mm});
            skCircle(sketch, "E11.0.2.4", {"center": v(276.23, 19.05) * mm, "radius": 1.49 * mm});
            skCircle(sketch, "E11.0.2.5", {"center": v(266.7, 38.1) * mm, "radius": 1.49 * mm});
            skCircle(sketch, "E11.0.2.6", {"center": v(155.57, 19.05) * mm, "radius": 1.49 * mm});
            skCircle(sketch, "E11.0.2.7", {"center": v(120.65, 19.05) * mm, "radius": 1.49 * mm});
            skCircle(sketch, "E11.0.2.8", {"center": v(260.35, 25.4) * mm, "radius": 1.49 * mm});
            skCircle(sketch, "E11.0.2.9", {"center": v(231.78, 19.05) * mm, "radius": 1.49 * mm});
            skCircle(sketch, "E11.0.2.10", {"center": v(184.15, 38.1) * mm, "radius": 1.49 * mm});
            skCircle(sketch, "E11.0.2.11", {"center": v(330.2, 31.75) * mm, "radius": 1.49 * mm});
            skCircle(sketch, "E11.0.2.12", {"center": v(282.58, 31.75) * mm, "radius": 1.49 * mm});
            skCircle(sketch, "E11.0.2.13", {"center": v(288.93, 31.75) * mm, "radius": 1.49 * mm});
            skCircle(sketch, "E11.0.2.14", {"center": v(120.65, 25.4) * mm, "radius": 1.49 * mm});
            skCircle(sketch, "E11.0.2.15", {"center": v(219.08, 19.05) * mm, "radius": 1.49 * mm});
            skCircle(sketch, "E11.0.2.16", {"center": v(196.85, 25.4) * mm, "radius": 1.49 * mm});
            skCircle(sketch, "E11.0.2.17", {"center": v(142.88, 25.4) * mm, "radius": 1.49 * mm});
            skCircle(sketch, "E11.0.2.18", {"center": v(330.2, 19.05) * mm, "radius": 1.49 * mm});
            skCircle(sketch, "E11.0.2.19", {"center": v(295.28, 38.1) * mm, "radius": 1.49 * mm});
            skCircle(sketch, "E11.0.2.20", {"center": v(155.57, 31.75) * mm, "radius": 1.49 * mm});
            skCircle(sketch, "E11.0.2.21", {"center": v(206.38, 19.05) * mm, "radius": 1.49 * mm});
            skCircle(sketch, "E11.0.2.22", {"center": v(196.85, 31.75) * mm, "radius": 1.49 * mm});
            skCircle(sketch, "E11.0.2.23", {"center": v(323.85, 25.4) * mm, "radius": 1.49 * mm});
            skCircle(sketch, "E11.0.2.24", {"center": v(276.23, 25.4) * mm, "radius": 1.49 * mm});
            skCircle(sketch, "E11.0.2.25", {"center": v(149.22, 25.4) * mm, "radius": 1.49 * mm});
            skCircle(sketch, "E11.0.2.26", {"center": v(260.35, 19.05) * mm, "radius": 1.49 * mm});
            skCircle(sketch, "E11.0.2.27", {"center": v(196.85, 38.1) * mm, "radius": 1.49 * mm});
            skCircle(sketch, "E11.0.2.28", {"center": v(323.85, 19.05) * mm, "radius": 1.49 * mm});
            skCircle(sketch, "E11.0.2.29", {"center": v(301.63, 25.4) * mm, "radius": 1.49 * mm});
            skCircle(sketch, "E11.0.2.30", {"center": v(149.22, 19.05) * mm, "radius": 1.49 * mm});
            skCircle(sketch, "E11.0.2.31", {"center": v(127, 25.4) * mm, "radius": 1.49 * mm});
            skCircle(sketch, "E11.0.2.32", {"center": v(101.6, 25.4) * mm, "radius": 1.49 * mm});
            skCircle(sketch, "E11.0.2.33", {"center": v(177.8, 19.05) * mm, "radius": 1.49 * mm});
            skCircle(sketch, "E11.0.2.34", {"center": v(336.55, 19.05) * mm, "radius": 1.49 * mm});
            skCircle(sketch, "E11.0.2.35", {"center": v(288.93, 38.1) * mm, "radius": 1.49 * mm});
            skCircle(sketch, "E11.0.2.36", {"center": v(254, 25.4) * mm, "radius": 1.49 * mm});
            skCircle(sketch, "E11.0.2.37", {"center": v(206.38, 25.4) * mm, "radius": 1.49 * mm});
            skCircle(sketch, "E11.0.2.38", {"center": v(190.5, 25.4) * mm, "radius": 1.49 * mm});
            skCircle(sketch, "E11.0.2.39", {"center": v(311.15, 19.05) * mm, "radius": 1.49 * mm});
            skCircle(sketch, "E11.0.2.40", {"center": v(161.92, 19.05) * mm, "radius": 1.49 * mm});
            skCircle(sketch, "E11.0.2.41", {"center": v(127, 19.05) * mm, "radius": 1.49 * mm});
            skCircle(sketch, "E11.0.2.42", {"center": v(101.6, 19.05) * mm, "radius": 1.49 * mm});
            skCircle(sketch, "E11.0.2.43", {"center": v(330.2, 38.1) * mm, "radius": 1.49 * mm});
            skCircle(sketch, "E11.0.2.44", {"center": v(301.63, 38.1) * mm, "radius": 1.49 * mm});
            skCircle(sketch, "E11.0.2.45", {"center": v(136.53, 19.05) * mm, "radius": 1.49 * mm});
            skCircle(sketch, "E11.0.2.46", {"center": v(254, 19.05) * mm, "radius": 1.49 * mm});
            skCircle(sketch, "E11.0.2.47", {"center": v(231.78, 25.4) * mm, "radius": 1.49 * mm});
            skCircle(sketch, "E11.0.2.48", {"center": v(177.8, 25.4) * mm, "radius": 1.49 * mm});
            skCircle(sketch, "E11.0.2.49", {"center": v(155.57, 38.1) * mm, "radius": 1.49 * mm});
            skCircle(sketch, "E11.0.2.50", {"center": v(266.7, 19.05) * mm, "radius": 1.49 * mm});
            skCircle(sketch, "E11.0.2.51", {"center": v(219.08, 38.1) * mm, "radius": 1.49 * mm});
            skCircle(sketch, "E11.0.2.52", {"center": v(190.5, 19.05) * mm, "radius": 1.49 * mm});
            skCircle(sketch, "E11.0.2.53", {"center": v(282.58, 19.05) * mm, "radius": 1.49 * mm});
            skCircle(sketch, "E11.0.2.54", {"center": v(241.3, 19.05) * mm, "radius": 1.49 * mm});
            skCircle(sketch, "E11.0.2.55", {"center": v(231.78, 31.75) * mm, "radius": 1.49 * mm});
            skCircle(sketch, "E11.0.2.56", {"center": v(190.5, 31.75) * mm, "radius": 1.49 * mm});
            skCircle(sketch, "E11.0.2.57", {"center": v(311.15, 25.4) * mm, "radius": 1.49 * mm});
            skCircle(sketch, "E11.0.2.58", {"center": v(295.28, 25.4) * mm, "radius": 1.49 * mm});
            skCircle(sketch, "E11.0.2.59", {"center": v(136.53, 25.4) * mm, "radius": 1.49 * mm});
            skCircle(sketch, "E11.0.2.60", {"center": v(107.95, 19.05) * mm, "radius": 1.49 * mm});
            skCircle(sketch, "E11.0.2.61", {"center": v(260.35, 38.1) * mm, "radius": 1.49 * mm});
            skCircle(sketch, "E11.0.2.62", {"center": v(231.78, 38.1) * mm, "radius": 1.49 * mm});
            skCircle(sketch, "E11.0.2.63", {"center": v(184.15, 25.4) * mm, "radius": 1.49 * mm});
            skCircle(sketch, "E11.0.2.64", {"center": v(336.55, 25.4) * mm, "radius": 1.49 * mm});
            skCircle(sketch, "E11.0.2.65", {"center": v(282.58, 25.4) * mm, "radius": 1.49 * mm});
            skCircle(sketch, "E11.0.2.66", {"center": v(161.92, 25.4) * mm, "radius": 1.49 * mm});
            skCircle(sketch, "E11.0.2.67", {"center": v(212.73, 19.05) * mm, "radius": 1.49 * mm});
            skCircle(sketch, "E11.0.2.68", {"center": v(184.15, 19.05) * mm, "radius": 1.49 * mm});
            skCircle(sketch, "E11.0.2.69", {"center": v(323.85, 38.1) * mm, "radius": 1.49 * mm});
            skCircle(sketch, "E11.0.2.70", {"center": v(225.43, 25.4) * mm, "radius": 1.49 * mm});
            skCircle(sketch, "E11.0.2.71", {"center": v(196.85, 19.05) * mm, "radius": 1.49 * mm});
            skCircle(sketch, "E11.0.2.72", {"center": v(149.22, 38.1) * mm, "radius": 1.49 * mm});
            skCircle(sketch, "E11.0.2.73", {"center": v(336.55, 31.75) * mm, "radius": 1.49 * mm});
            skCircle(sketch, "E11.0.2.74", {"center": v(295.28, 31.75) * mm, "radius": 1.49 * mm});
            skCircle(sketch, "E11.0.2.75", {"center": v(241.3, 25.4) * mm, "radius": 1.49 * mm});
            skCircle(sketch, "E11.0.2.76", {"center": v(114.3, 25.4) * mm, "radius": 1.49 * mm});
            skCircle(sketch, "E11.0.2.77", {"center": v(212.73, 25.4) * mm, "radius": 1.49 * mm});
            skCircle(sketch, "E11.0.2.78", {"center": v(171.45, 19.05) * mm, "radius": 1.49 * mm});
            skCircle(sketch, "E11.0.2.79", {"center": v(336.55, 38.1) * mm, "radius": 1.49 * mm});
            skCircle(sketch, "E11.0.2.80", {"center": v(288.93, 25.4) * mm, "radius": 1.49 * mm});
            skCircle(sketch, "E11.0.2.81", {"center": v(266.7, 25.4) * mm, "radius": 1.49 * mm});
            skCircle(sketch, "E11.0.2.82", {"center": v(190.5, 38.1) * mm, "radius": 1.49 * mm});
            skCircle(sketch, "E11.0.2.83", {"center": v(161.92, 38.1) * mm, "radius": 1.49 * mm});
            skCircle(sketch, "E11.0.2.84", {"center": v(317.5, 19.05) * mm, "radius": 1.49 * mm});
            skCircle(sketch, "E11.0.2.85", {"center": v(288.93, 19.05) * mm, "radius": 1.49 * mm});
            skCircle(sketch, "E11.0.2.86", {"center": v(254, 38.1) * mm, "radius": 1.49 * mm});
            skCircle(sketch, "E11.0.2.87", {"center": v(330.2, 25.4) * mm, "radius": 1.49 * mm});
            skCircle(sketch, "E11.0.2.88", {"center": v(301.63, 19.05) * mm, "radius": 1.49 * mm});
            skCircle(sketch, "E11.0.2.89", {"center": v(266.7, 31.75) * mm, "radius": 1.49 * mm});
            skCircle(sketch, "E11.0.2.90", {"center": v(120.65, 31.75) * mm, "radius": 1.49 * mm});
            skCircle(sketch, "E11.0.2.91", {"center": v(171.45, 31.75) * mm, "radius": 1.49 * mm});
            skLineSegment(sketch, "E11.0.2.92", {"start": v(114.3, 31.75) * mm, "end": v(149.22, 31.75) * mm, "construction": true});
            skCircle(sketch, "E11.0.2.93", {"center": v(247.65, 19.05) * mm, "radius": 1.49 * mm});
            skCircle(sketch, "E11.0.2.94", {"center": v(127, 38.1) * mm, "radius": 1.49 * mm});
            skCircle(sketch, "E11.0.2.95", {"center": v(247.65, 25.4) * mm, "radius": 1.49 * mm});
            skCircle(sketch, "E11.0.2.96", {"center": v(127, 31.75) * mm, "radius": 1.49 * mm});
            skCircle(sketch, "E11.0.2.97", {"center": v(225.43, 38.1) * mm, "radius": 1.49 * mm});
            skCircle(sketch, "E11.0.2.98", {"center": v(282.58, 38.1) * mm, "radius": 1.49 * mm});
            skCircle(sketch, "E11.0.2.99", {"center": v(260.35, 31.75) * mm, "radius": 1.49 * mm});
            skCircle(sketch, "E11.0.2.100", {"center": v(212.73, 31.75) * mm, "radius": 1.49 * mm});
            skCircle(sketch, "E11.0.2.101", {"center": v(219.08, 31.75) * mm, "radius": 1.49 * mm});
            skCircle(sketch, "E11.0.2.102", {"center": v(301.63, 31.75) * mm, "radius": 1.49 * mm});
            skCircle(sketch, "E11.0.2.103", {"center": v(212.73, 38.1) * mm, "radius": 1.49 * mm});
            skCircle(sketch, "E11.0.2.104", {"center": v(323.85, 31.75) * mm, "radius": 1.49 * mm});
            skCircle(sketch, "E11.0.2.105", {"center": v(142.88, 31.75) * mm, "radius": 1.49 * mm});
            skCircle(sketch, "E11.0.2.106", {"center": v(149.22, 31.75) * mm, "radius": 1.49 * mm});
            skCircle(sketch, "E11.0.2.107", {"center": v(107.95, 25.4) * mm, "radius": 1.49 * mm});
            skCircle(sketch, "E11.0.2.108", {"center": v(247.65, 31.75) * mm, "radius": 1.49 * mm});
            skCircle(sketch, "E11.0.2.109", {"center": v(254, 31.75) * mm, "radius": 1.49 * mm});
            skCircle(sketch, "E11.0.2.110", {"center": v(295.28, 19.05) * mm, "radius": 1.49 * mm});
            skCircle(sketch, "E11.0.2.111", {"center": v(114.3, 31.75) * mm, "radius": 1.49 * mm});
            skCircle(sketch, "E11.0.2.112", {"center": v(241.3, 31.75) * mm, "radius": 1.49 * mm});
            skCircle(sketch, "E11.0.2.113", {"center": v(161.92, 31.75) * mm, "radius": 1.49 * mm});
            skCircle(sketch, "E11.0.2.114", {"center": v(114.3, 19.05) * mm, "radius": 1.49 * mm});
            skCircle(sketch, "E11.0.2.115", {"center": v(225.43, 19.05) * mm, "radius": 1.49 * mm});
            skCircle(sketch, "E11.0.2.116", {"center": v(120.65, 38.1) * mm, "radius": 1.49 * mm});
            skCircle(sketch, "E11.0.2.117", {"center": v(225.43, 31.75) * mm, "radius": 1.49 * mm});
            skCircle(sketch, "E11.0.2.118", {"center": v(177.8, 31.75) * mm, "radius": 1.49 * mm});
            skCircle(sketch, "E11.0.2.119", {"center": v(184.15, 31.75) * mm, "radius": 1.49 * mm});
            skCircle(sketch, "E11.0.2.120", {"center": v(142.88, 19.05) * mm, "radius": 1.49 * mm});
            skLineSegment(sketch, "E11.0.2.121", {"start": v(171.45, 38.1) * mm, "end": v(171.45, 31.75) * mm, "construction": true});
            skCircle(sketch, "E11.0.2.122", {"center": v(177.8, 38.1) * mm, "radius": 1.49 * mm});
            skCircle(sketch, "E11.0.2.123", {"center": v(171.45, 38.1) * mm, "radius": 1.49 * mm});
            skCircle(sketch, "E11.0.2.124", {"center": v(276.23, 31.75) * mm, "radius": 1.49 * mm});
            skCircle(sketch, "E11.0.2.125", {"center": v(101.6, 31.75) * mm, "radius": 1.49 * mm});
            skLineSegment(sketch, "E11.0.2.126", {"start": v(171.45, 38.1) * mm, "end": v(177.8, 38.1) * mm, "construction": true});
            skLineSegment(sketch, "E11.0.2.127", {"start": v(276.23, 38.1) * mm, "end": v(276.23, 31.75) * mm, "construction": true});
            skCircle(sketch, "E11.0.2.128", {"center": v(206.38, 31.75) * mm, "radius": 1.49 * mm});
            skCircle(sketch, "E11.0.2.129", {"center": v(276.23, 38.1) * mm, "radius": 1.49 * mm});
            skLineSegment(sketch, "E11.0.2.130", {"start": v(276.23, 38.1) * mm, "end": v(282.58, 38.1) * mm, "construction": true});
            skCircle(sketch, "E11.0.2.131", {"center": v(107.95, 38.1) * mm, "radius": 1.49 * mm});
            skCircle(sketch, "E11.0.2.132", {"center": v(107.95, 31.75) * mm, "radius": 1.49 * mm});
            skCircle(sketch, "E11.0.2.133", {"center": v(317.5, 31.75) * mm, "radius": 1.49 * mm});
            skCircle(sketch, "E11.0.2.134", {"center": v(206.38, 38.1) * mm, "radius": 1.49 * mm});
            skCircle(sketch, "E11.0.2.135", {"center": v(311.15, 31.75) * mm, "radius": 1.49 * mm});
            skCircle(sketch, "E11.0.2.136", {"center": v(136.53, 31.75) * mm, "radius": 1.49 * mm});
            skLineSegment(sketch, "E11.0.2.137", {"start": v(206.38, 38.1) * mm, "end": v(212.72, 38.1) * mm, "construction": true});
            skCircle(sketch, "E11.0.2.138", {"center": v(317.5, 38.1) * mm, "radius": 1.49 * mm});
            skCircle(sketch, "E11.0.2.139", {"center": v(142.88, 38.1) * mm, "radius": 1.49 * mm});
            skCircle(sketch, "E11.0.2.140", {"center": v(114.3, 38.1) * mm, "radius": 1.49 * mm});
            skLineSegment(sketch, "E11.0.2.141", {"start": v(311.15, 38.1) * mm, "end": v(311.15, 31.75) * mm, "construction": true});
            skCircle(sketch, "E11.0.2.142", {"center": v(311.15, 38.1) * mm, "radius": 1.49 * mm});
            skCircle(sketch, "E11.0.2.143", {"center": v(247.65, 38.1) * mm, "radius": 1.49 * mm});
            skLineSegment(sketch, "E11.0.2.144", {"start": v(311.15, 38.1) * mm, "end": v(317.5, 38.1) * mm, "construction": true});
            skLineSegment(sketch, "E11.0.2.145", {"start": v(241.3, 38.1) * mm, "end": v(241.3, 31.75) * mm, "construction": true});
            skCircle(sketch, "E11.0.2.146", {"center": v(241.3, 38.1) * mm, "radius": 1.49 * mm});
            skLineSegment(sketch, "E11.0.2.147", {"start": v(241.3, 38.1) * mm, "end": v(247.65, 38.1) * mm, "construction": true});
            skCircle(sketch, "E11.0.2.148", {"center": v(101.6, 38.1) * mm, "radius": 1.49 * mm});
            skLineSegment(sketch, "E11.0.2.149", {"start": v(101.6, 38.1) * mm, "end": v(107.95, 38.1) * mm, "construction": true});
            skLineSegment(sketch, "E11.0.2.150", {"start": v(101.6, 38.1) * mm, "end": v(101.6, 31.75) * mm, "construction": true});
            skLineSegment(sketch, "E11.0.2.151", {"start": v(206.38, 38.1) * mm, "end": v(206.38, 31.75) * mm, "construction": true});
            skLineSegment(sketch, "E11.0.2.152", {"start": v(136.53, 38.1) * mm, "end": v(136.53, 31.75) * mm, "construction": true});
            skCircle(sketch, "E11.0.2.153", {"center": v(136.53, 38.1) * mm, "radius": 1.49 * mm});
            skLineSegment(sketch, "E11.0.2.154", {"start": v(136.53, 38.1) * mm, "end": v(142.87, 38.1) * mm, "construction": true});
            skLineSegment(sketch, "E11.direction1", {"start": v(219.08, 107.95) * mm, "end": v(244.48, 107.95) * mm, "construction": true});
            skLineSegment(sketch, "E11.direction2", {"start": v(219.08, 107.95) * mm, "end": v(219.08, 66.68) * mm, "construction": true});
            skCircle(sketch, "E12", {"center": v(346.07, 120.65) * mm, "radius": 1.49 * mm});
            skLineSegment(sketch, "E13", {"start": v(419.1, 69.85) * mm, "end": v(346.07, 69.85) * mm});
            skLineSegment(sketch, "E14", {"start": v(346.07, 120.65) * mm, "end": v(346.07, 0) * mm});
            skCircle(sketch, "E15", {"center": v(346.07, 114.3) * mm, "radius": 1.49 * mm});
            skCircle(sketch, "E16", {"center": v(346.07, 107.95) * mm, "radius": 1.49 * mm});
            skCircle(sketch, "E17", {"center": v(346.07, 101.6) * mm, "radius": 1.49 * mm});
            skCircle(sketch, "E18.1.0", {"center": v(356.93, 99.69) * mm, "radius": 1.49 * mm});
            skCircle(sketch, "E18.1.1", {"center": v(359.1, 105.65) * mm, "radius": 1.49 * mm});
            skCircle(sketch, "E18.1.2", {"center": v(361.28, 111.62) * mm, "radius": 1.49 * mm});
            skCircle(sketch, "E18.1.3", {"center": v(363.45, 117.59) * mm, "radius": 1.49 * mm});
            skCircle(sketch, "E18.2.0", {"center": v(366.48, 94.17) * mm, "radius": 1.49 * mm});
            skCircle(sketch, "E18.2.1", {"center": v(370.57, 99.04) * mm, "radius": 1.49 * mm});
            skCircle(sketch, "E18.2.2", {"center": v(374.65, 103.9) * mm, "radius": 1.49 * mm});
            skCircle(sketch, "E18.2.3", {"center": v(378.73, 108.77) * mm, "radius": 1.49 * mm});
            skCircle(sketch, "E18.3.0", {"center": v(373.57, 85.73) * mm, "radius": 1.49 * mm});
            skCircle(sketch, "E18.3.1", {"center": v(379.07, 88.9) * mm, "radius": 1.49 * mm});
            skCircle(sketch, "E18.3.2", {"center": v(384.57, 92.08) * mm, "radius": 1.49 * mm});
            skCircle(sketch, "E18.3.3", {"center": v(390.07, 95.25) * mm, "radius": 1.49 * mm});
            skCircle(sketch, "E18.4.0", {"center": v(377.34, 75.36) * mm, "radius": 1.49 * mm});
            skCircle(sketch, "E18.4.1", {"center": v(383.6, 76.47) * mm, "radius": 1.49 * mm});
            skCircle(sketch, "E18.4.2", {"center": v(389.85, 77.57) * mm, "radius": 1.49 * mm});
            skCircle(sketch, "E18.4.3", {"center": v(396.1, 78.67) * mm, "radius": 1.49 * mm});
            skCircle(sketch, "E18.5.0", {"center": v(377.34, 64.34) * mm, "radius": 1.49 * mm});
            skCircle(sketch, "E18.5.1", {"center": v(383.6, 63.23) * mm, "radius": 1.49 * mm});
            skCircle(sketch, "E18.5.2", {"center": v(389.85, 62.13) * mm, "radius": 1.49 * mm});
            skCircle(sketch, "E18.5.3", {"center": v(396.1, 61.03) * mm, "radius": 1.49 * mm});
            skCircle(sketch, "E18.6.0", {"center": v(373.57, 53.97) * mm, "radius": 1.49 * mm});
            skCircle(sketch, "E18.6.1", {"center": v(379.07, 50.8) * mm, "radius": 1.49 * mm});
            skCircle(sketch, "E18.6.2", {"center": v(384.57, 47.63) * mm, "radius": 1.49 * mm});
            skCircle(sketch, "E18.6.3", {"center": v(390.07, 44.45) * mm, "radius": 1.49 * mm});
            skCircle(sketch, "E18.7.0", {"center": v(366.48, 45.53) * mm, "radius": 1.49 * mm});
            skCircle(sketch, "E18.7.1", {"center": v(370.57, 40.66) * mm, "radius": 1.49 * mm});
            skCircle(sketch, "E18.7.2", {"center": v(374.65, 35.8) * mm, "radius": 1.49 * mm});
            skCircle(sketch, "E18.7.3", {"center": v(378.73, 30.93) * mm, "radius": 1.49 * mm});
            skCircle(sketch, "E18.8.0", {"center": v(356.93, 40.01) * mm, "radius": 1.49 * mm});
            skCircle(sketch, "E18.8.1", {"center": v(359.1, 34.05) * mm, "radius": 1.49 * mm});
            skCircle(sketch, "E18.8.2", {"center": v(361.28, 28.08) * mm, "radius": 1.49 * mm});
            skCircle(sketch, "E18.8.3", {"center": v(363.45, 22.11) * mm, "radius": 1.49 * mm});
            skCircle(sketch, "E18.9.0", {"center": v(346.07, 38.1) * mm, "radius": 1.49 * mm});
            skCircle(sketch, "E18.9.1", {"center": v(346.07, 31.75) * mm, "radius": 1.49 * mm});
            skCircle(sketch, "E18.9.2", {"center": v(346.07, 25.4) * mm, "radius": 1.49 * mm});
            skCircle(sketch, "E18.9.3", {"center": v(346.07, 19.05) * mm, "radius": 1.49 * mm});
            skPoint(sketch, "E18.center", {"position": v(346.07, 69.85) * mm});
            skLineSegment(sketch, "E18.anchor1", {"start": v(346.07, 69.85) * mm, "end": v(346.07, 101.6) * mm, "construction": true});
            skLineSegment(sketch, "E18.anchor2", {"start": v(346.07, 69.85) * mm, "end": v(346.07, 38.1) * mm, "construction": true});
            skCircle(sketch, "E19", {"center": v(92.07, 19.05) * mm, "radius": 1.49 * mm});
            skCircle(sketch, "E20", {"center": v(92.07, 25.4) * mm, "radius": 1.49 * mm});
            skCircle(sketch, "E21", {"center": v(92.07, 31.75) * mm, "radius": 1.49 * mm});
            skCircle(sketch, "E22", {"center": v(92.07, 38.1) * mm, "radius": 1.49 * mm});
            skLineSegment(sketch, "E23", {"start": v(92.07, 38.1) * mm, "end": v(92.07, 49.21) * mm});
            skCircle(sketch, "E24.1.0", {"center": v(84.22, 41.35) * mm, "radius": 1.49 * mm});
            skCircle(sketch, "E24.1.1", {"center": v(79.73, 36.86) * mm, "radius": 1.49 * mm});
            skCircle(sketch, "E24.1.2", {"center": v(75.24, 32.37) * mm, "radius": 1.49 * mm});
            skCircle(sketch, "E24.1.3", {"center": v(70.75, 27.88) * mm, "radius": 1.49 * mm});
            skCircle(sketch, "E24.2.0", {"center": v(80.96, 49.21) * mm, "radius": 1.49 * mm});
            skCircle(sketch, "E24.2.1", {"center": v(74.61, 49.21) * mm, "radius": 1.49 * mm});
            skCircle(sketch, "E24.2.2", {"center": v(68.26, 49.21) * mm, "radius": 1.49 * mm});
            skCircle(sketch, "E24.2.3", {"center": v(61.91, 49.21) * mm, "radius": 1.49 * mm});
            skCircle(sketch, "E24.3.0", {"center": v(84.22, 57.07) * mm, "radius": 1.49 * mm});
            skCircle(sketch, "E24.3.1", {"center": v(79.73, 61.56) * mm, "radius": 1.49 * mm});
            skCircle(sketch, "E24.3.2", {"center": v(75.24, 66.05) * mm, "radius": 1.49 * mm});
            skCircle(sketch, "E24.3.3", {"center": v(70.75, 70.54) * mm, "radius": 1.49 * mm});
            skCircle(sketch, "E24.4.0", {"center": v(92.07, 60.33) * mm, "radius": 1.49 * mm});
            skCircle(sketch, "E24.4.1", {"center": v(92.07, 66.68) * mm, "radius": 1.49 * mm});
            skCircle(sketch, "E24.4.2", {"center": v(92.07, 73.03) * mm, "radius": 1.49 * mm});
            skCircle(sketch, "E24.4.3", {"center": v(92.07, 79.38) * mm, "radius": 1.49 * mm});
            skPoint(sketch, "E24.center", {"position": v(92.07, 49.21) * mm});
            skLineSegment(sketch, "E24.anchor1", {"start": v(92.07, 49.21) * mm, "end": v(92.07, 38.1) * mm, "construction": true});
            skLineSegment(sketch, "E24.anchor2", {"start": v(92.07, 49.21) * mm, "end": v(92.07, 60.33) * mm, "construction": true});
            skCircle(sketch, "E25", {"center": v(355.6, 69.85) * mm, "radius": 1.49 * mm});
            skSolve(sketch);
        }
        {
            var Q0;
            Q0=qSketchRegion(id+"F2",true);
            extrude(context, id + "F3", {"entities" : qUnion([Q0]), "operationType" : NewBodyOperationType.REMOVE, "oppositeDirection" : true, "depth" : 12.7 * mm});
        }
    });
